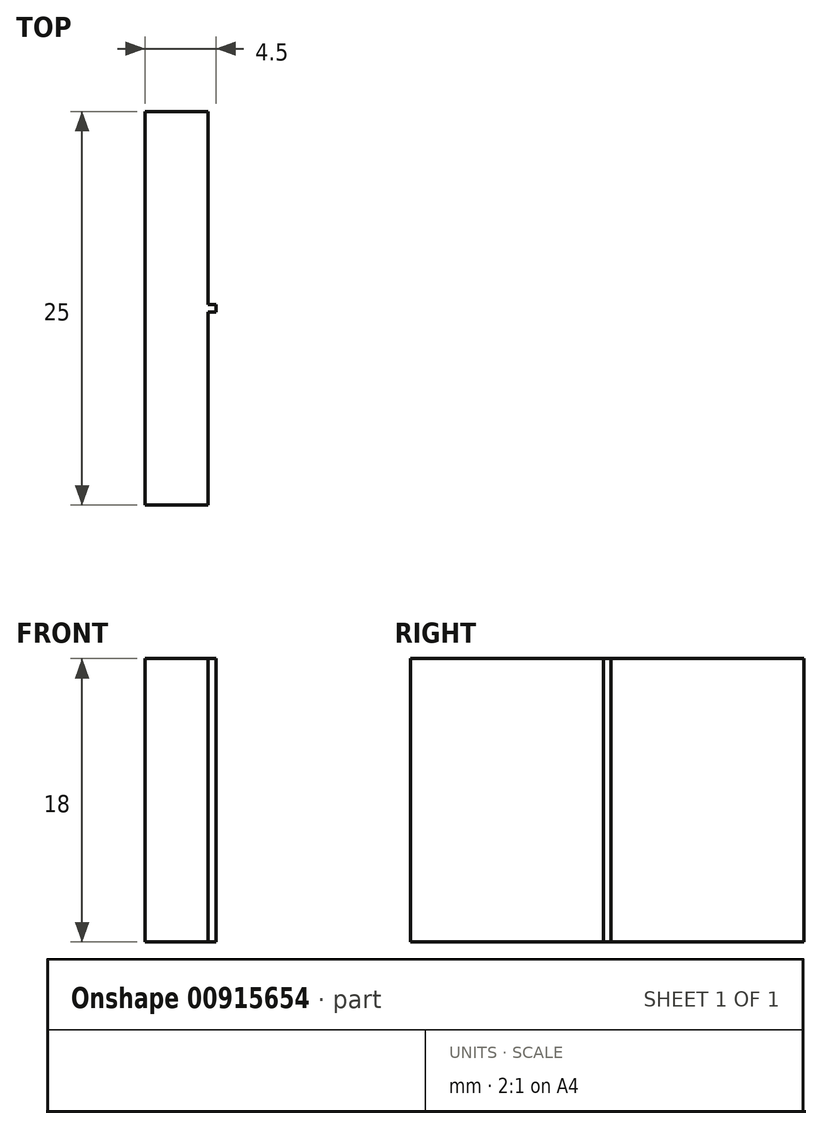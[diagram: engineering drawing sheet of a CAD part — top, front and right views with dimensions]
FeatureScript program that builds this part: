
annotation { "Feature Type Name" : "Feature", "Feature Type Description" : "" }
export const myFeature = defineFeature(function(context is Context, id is Id, definition is map)
    precondition{}
    {
        {
            var Q0;
            Q0=qCreatedBy(makeId("Top.planeOp"),FACE);
            var sketch = newSketch(context, id + "F0", { "sketchPlane" : qUnion([Q0])});
            skLineSegment(sketch, "E0", {"start": v(0, -12.5) * mm, "end": v(0, 12.5) * mm});
            skLineSegment(sketch, "E1", {"start": v(0, 12.5) * mm, "end": v(4, 12.5) * mm});
            skLineSegment(sketch, "E2", {"start": v(4, 12.5) * mm, "end": v(4, 0.25) * mm});
            skLineSegment(sketch, "E3", {"start": v(4, 0.25) * mm, "end": v(4.5, 0.25) * mm});
            skLineSegment(sketch, "E4", {"start": v(4.5, 0.25) * mm, "end": v(4.5, -0.25) * mm});
            skLineSegment(sketch, "E5", {"start": v(4.5, -0.25) * mm, "end": v(4, -0.25) * mm});
            skLineSegment(sketch, "E6", {"start": v(4, -0.25) * mm, "end": v(4, -12.5) * mm});
            skLineSegment(sketch, "E7", {"start": v(4, -12.5) * mm, "end": v(0, -12.5) * mm});
            skSolve(sketch);
        }
        {
            var Q0;
            Q0 = qSketchRegion(id + "F0", true);
            extrude(context, id + "F1", {"entities" : qUnion([Q0]), "depth" : 18 * mm, "offsetDistance" : 25.4 * mm});
        }
    });
